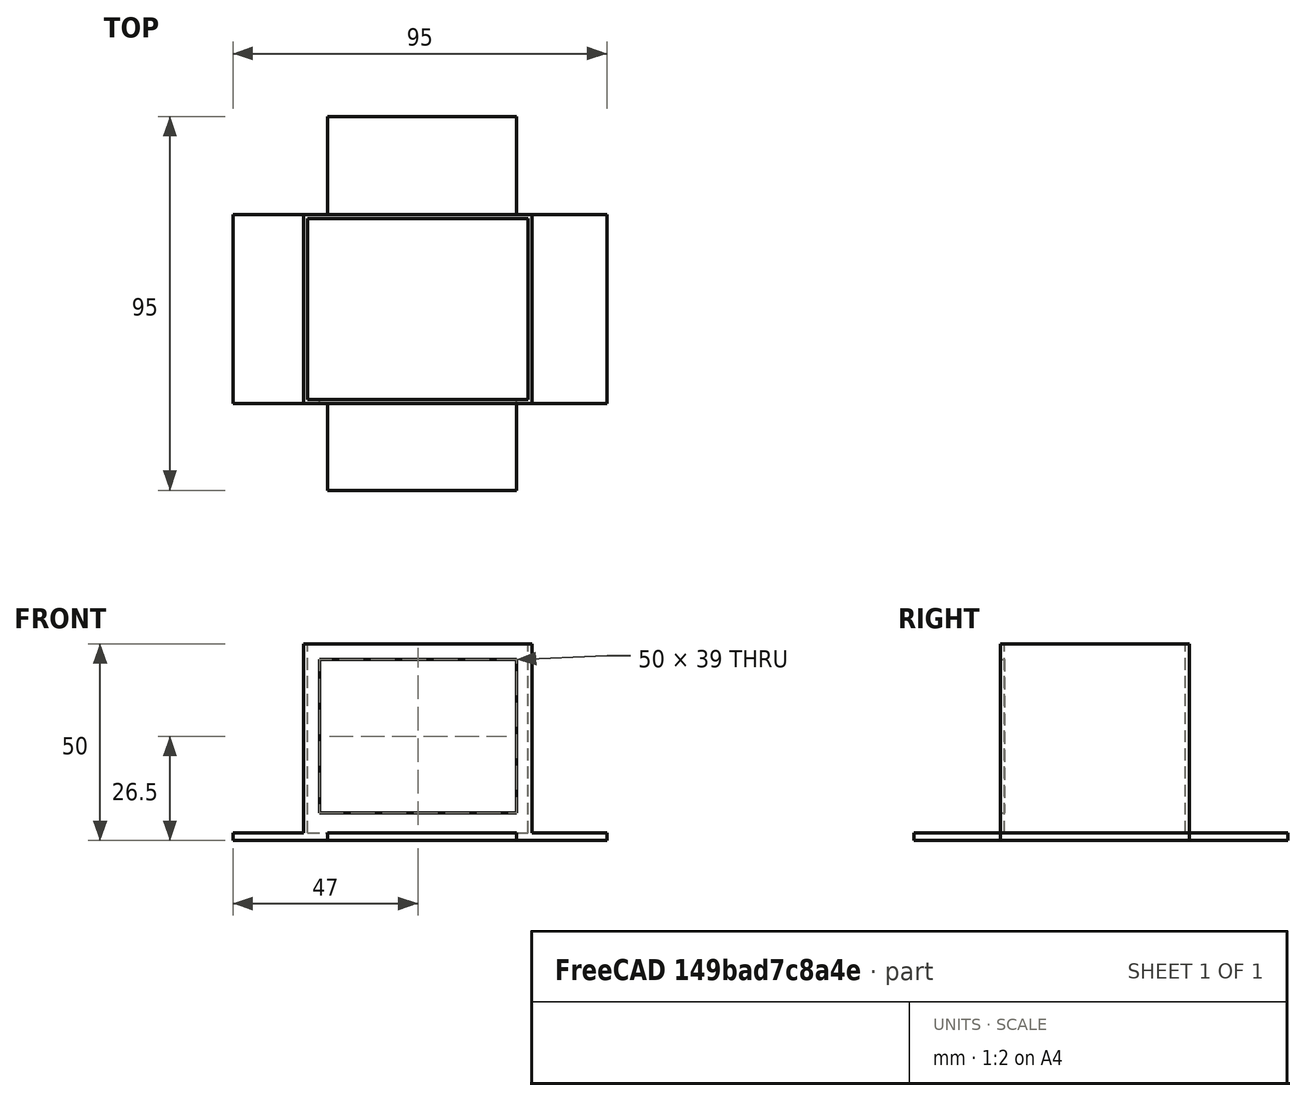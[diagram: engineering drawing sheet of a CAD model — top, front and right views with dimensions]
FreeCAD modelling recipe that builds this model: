
FCSTD DOCUMENT  (FreeCAD 0.15R4671 (Git))
Label: robotspeaker
License: All rights reserved
LicenseURL: http://en.wikipedia.org/wiki/All_rights_reserved
objects: Part::Box×5, Part::Cut×2, Part::MultiFuse×1
note: 8 computed .brp shape members not serialized (recipe doc carries the construction recipe); baked Part::Feature solids carry a one-line shape summary decoded from their .brp

FEATURE [Part::Box] Box  label="Cube"
  Height = 50
  Length = 58
  Width = 48
FEATURE [Part::Box] Box001  label="Cube001"
  Height = 59
  Length = 56
  Placement = pos=(1,1,2) rot=(0,0,1;0rad)
  Width = 46
FEATURE [Part::Cut] Cut
  Base = -> Box
  Tool = -> Box001
FEATURE [Part::Box] Box002  label="Cube002"
  Height = 39
  Length = 50
  Placement = pos=(4,-2,7) rot=(0,0,1;0rad)
  Width = 13
FEATURE [Part::Cut] Cut001
  Base = -> Cut
  Tool = -> Box002
FEATURE [Part::Box] Box003  label="Cube003"
  Height = 2
  Length = 95
  Placement = pos=(-18,0,0) rot=(0,0,1;0rad)
  Width = 48
FEATURE [Part::Box] Box004  label="Cube004"
  Height = 2
  Length = 95
  Placement = pos=(54,-22,0) rot=(0,0,1;1.5708rad)
  Width = 48
FEATURE [Part::MultiFuse] Fusion
  Shapes = -> [Cut001,Box003,Box004]
